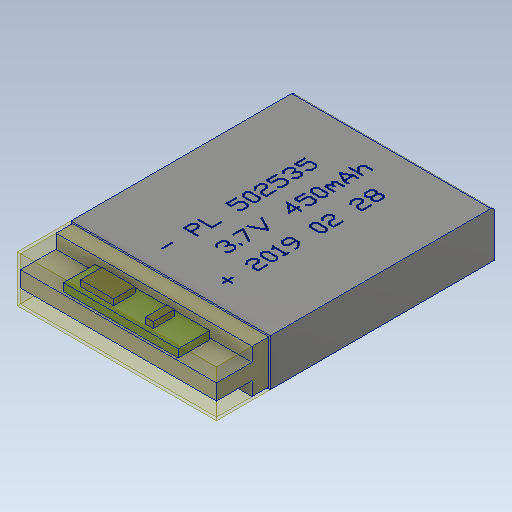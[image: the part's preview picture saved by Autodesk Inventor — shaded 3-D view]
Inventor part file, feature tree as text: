
AUTODESK INVENTOR PART (.ipt)
format: ipt  version: 2020.1 (Build 241239000, 239)  size: 667,648 bytes
history: native  units: mm
features: extrude x7, sketch x5, plane x1, emboss x1, fillet x1, projected_geometry x1
ambient origin geometry x8: Origin, YZ Plane, XZ Plane, XY Plane, X Axis, Y Axis, Z Axis, Center Point
bodies: Solid1 (feature_tree), Solid3 (feature_tree)
feature tree (16):
  sketch  "Sketch1"  dims[d1=35.0mm d2=4.5mm]
  extrude  "Extrusion1"  Depth=4.5mm
  extrude  "Extrusion2"  Depth=2.0mm TaperAngle=0.0deg
  plane  "Work Plane1"
  sketch  "Sketch3"  dims[d3=5.9mm d4=0.0mm d5=2.0mm d6=0.0mm]
  extrude  "Extrusion4"  Depth=25.0mm
  extrude  "Extrusion5"  Depth=0.2mm
  extrude  "Extrusion6"  Depth=10.0mm TaperAngle=0.0deg
  extrude  "Extrusion7"  Depth=0.2mm TaperAngle=0.0deg
  extrude  "Extrusion8"  Depth=14.5mm
  emboss  "Emboss1"
  fillet  "Fillet3"  Radius=4.0mm
  projected_geometry  "Projected Loop2"
  sketch  "Sketch4"  dims[d12=25.2mm d13=25.0mm]
  sketch  "Sketch5"  dims[d16=0.2mm d17=0.2mm]
  sketch  "Sketch6"  dims[d18=6.8mm d19=0.0mm d20=10.0mm d21=0.0mm d22=0.2mm d23=0.0mm d24=14.5mm d25=4.0mm d26=24.8mm d27=12.4mm d28=0.2mm d29=1.0mm d30=0.0mm d31=1.0mm d33=4.2mm d34=2.7mm d35=2.0mm d36=3.8mm d37=1.5mm d38=0.5mm d39=0.0mm d40=2.5mm d41=0.001mm d42=0.0mm d43=0.5mm]
